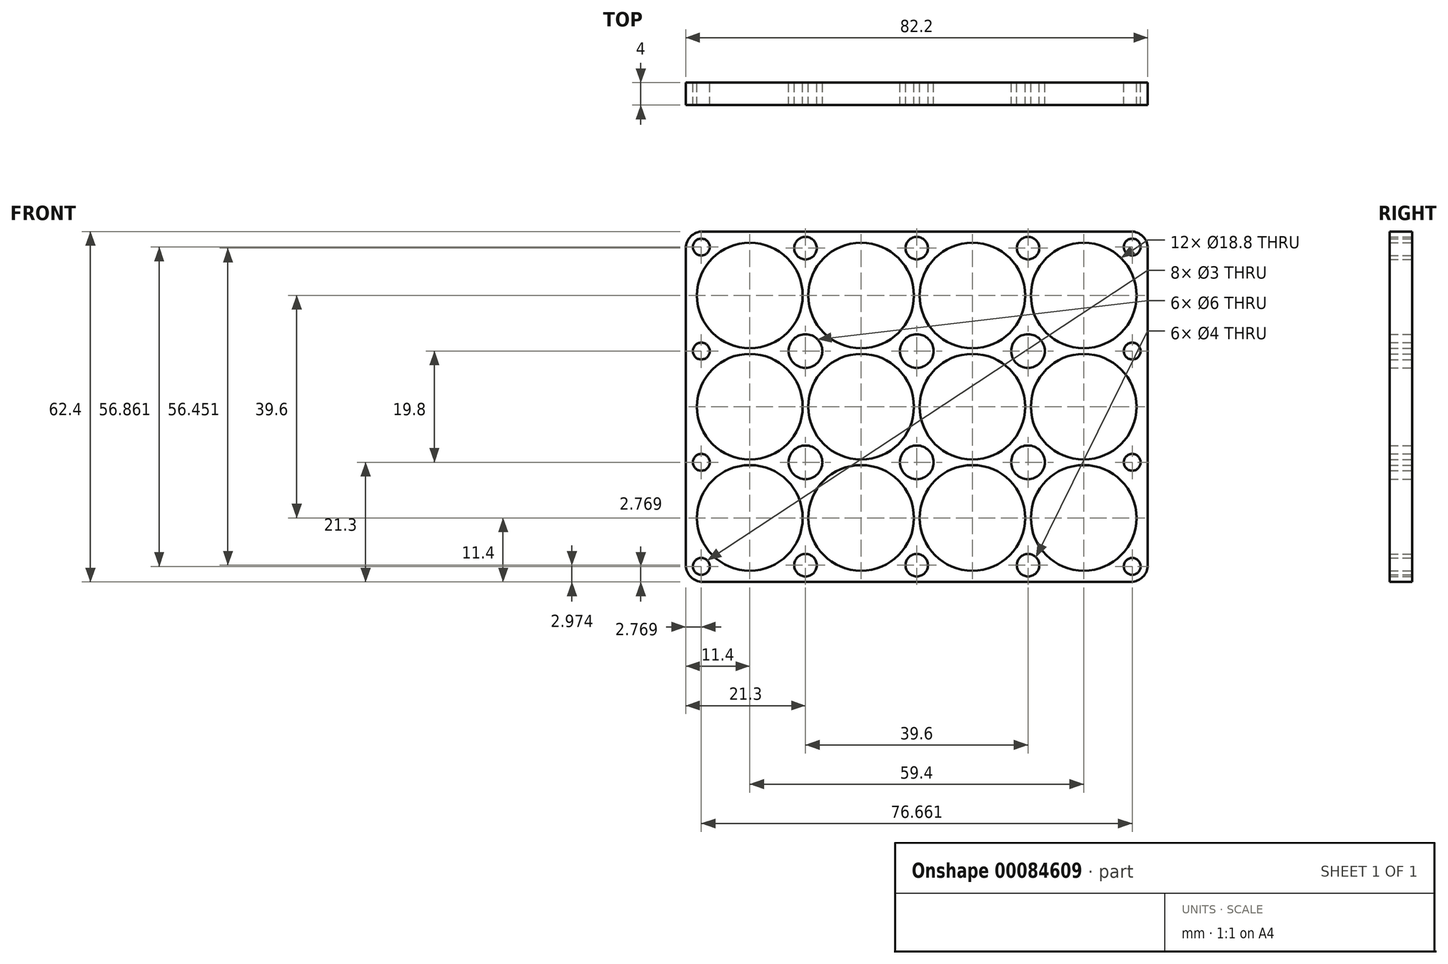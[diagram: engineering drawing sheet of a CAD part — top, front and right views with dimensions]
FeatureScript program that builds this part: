
annotation { "Feature Type Name" : "Feature", "Feature Type Description" : "" }
export const myFeature = defineFeature(function(context is Context, id is Id, definition is map)
    precondition{}
    {
        {
            var Q0;
            Q0=qCreatedBy(makeId("Front.planeOp"),FACE);
            var sketch = newSketch(context, id + "F0", { "sketchPlane" : qUnion([Q0]) });
            skCircle(sketch, "E0", {"center": v(0, 0) * mm, "radius": 9.4 * mm});
            skCircle(sketch, "E1.0.1.0", {"center": v(0, 19.8) * mm, "radius": 9.4 * mm});
            skCircle(sketch, "E1.0.2.0", {"center": v(0, 39.6) * mm, "radius": 9.4 * mm});
            skCircle(sketch, "E1.1.0.0", {"center": v(19.8, 0) * mm, "radius": 9.4 * mm});
            skCircle(sketch, "E1.1.1.0", {"center": v(19.8, 19.8) * mm, "radius": 9.4 * mm});
            skCircle(sketch, "E1.1.2.0", {"center": v(19.8, 39.6) * mm, "radius": 9.4 * mm});
            skCircle(sketch, "E1.2.0.0", {"center": v(39.6, 0) * mm, "radius": 9.4 * mm});
            skCircle(sketch, "E1.2.1.0", {"center": v(39.6, 19.8) * mm, "radius": 9.4 * mm});
            skCircle(sketch, "E1.2.2.0", {"center": v(39.6, 39.6) * mm, "radius": 9.4 * mm});
            skCircle(sketch, "E1.3.0.0", {"center": v(59.4, 0) * mm, "radius": 9.4 * mm});
            skCircle(sketch, "E1.3.1.0", {"center": v(59.4, 19.8) * mm, "radius": 9.4 * mm});
            skCircle(sketch, "E1.3.2.0", {"center": v(59.4, 39.6) * mm, "radius": 9.4 * mm});
            skLineSegment(sketch, "E1.direction1", {"start": v(0, 0) * mm, "end": v(19.8, 0) * mm, "construction": true});
            skLineSegment(sketch, "E1.direction2", {"start": v(0, 0) * mm, "end": v(0, 19.8) * mm, "construction": true});
            skLineSegment(sketch, "E2", {"start": v(-9.4, 19.8) * mm, "end": v(68.8, 19.8) * mm, "construction": true});
            skLineSegment(sketch, "E3", {"start": v(29.7, 19.8) * mm, "end": v(29.7, -16.3) * mm, "construction": true});
            skLineSegment(sketch, "E4.bottom", {"start": v(70.8, -11.4) * mm, "end": v(-11.4, -11.4) * mm});
            skLineSegment(sketch, "E4.top", {"start": v(70.8, 51) * mm, "end": v(-11.4, 51) * mm});
            skLineSegment(sketch, "E4.left", {"start": v(70.8, -11.4) * mm, "end": v(70.8, 51) * mm});
            skLineSegment(sketch, "E4.right", {"start": v(-11.4, -11.4) * mm, "end": v(-11.4, 51) * mm});
            skPoint(sketch, "E4.middle", {"position": v(29.7, 19.8) * mm});
            skLineSegment(sketch, "E5", {"start": v(19.8, 19.8) * mm, "end": v(0, 0) * mm, "construction": true});
            skLineSegment(sketch, "E6", {"start": v(19.8, 0) * mm, "end": v(0, 19.8) * mm, "construction": true});
            skCircle(sketch, "E7", {"center": v(9.9, 9.9) * mm, "radius": 3 * mm});
            skCircle(sketch, "E8.0.1.0", {"center": v(9.9, 29.7) * mm, "radius": 3 * mm});
            skCircle(sketch, "E8.1.0.0", {"center": v(29.7, 9.9) * mm, "radius": 3 * mm});
            skCircle(sketch, "E8.1.1.0", {"center": v(29.7, 29.7) * mm, "radius": 3 * mm});
            skCircle(sketch, "E8.2.0.0", {"center": v(49.5, 9.9) * mm, "radius": 3 * mm});
            skCircle(sketch, "E8.2.1.0", {"center": v(49.5, 29.7) * mm, "radius": 3 * mm});
            skLineSegment(sketch, "E8.direction1", {"start": v(9.9, 9.9) * mm, "end": v(29.7, 9.9) * mm, "construction": true});
            skLineSegment(sketch, "E8.direction2", {"start": v(9.9, 9.9) * mm, "end": v(9.9, 29.7) * mm, "construction": true});
            skLineSegment(sketch, "E9", {"start": v(9.9, 0) * mm, "end": v(9.9, -11.4) * mm, "construction": true});
            skCircle(sketch, "E10", {"center": v(9.9, -8.43) * mm, "radius": 2 * mm});
            skCircle(sketch, "E11.1.0.0", {"center": v(29.7, -8.43) * mm, "radius": 2 * mm});
            skCircle(sketch, "E11.2.0.0", {"center": v(49.5, -8.43) * mm, "radius": 2 * mm});
            skLineSegment(sketch, "E11.direction1", {"start": v(9.9, -8.43) * mm, "end": v(29.7, -8.43) * mm, "construction": true});
            skCircle(sketch, "E12.MirrorC", {"center": v(9.9, 48.03) * mm, "radius": 2 * mm});
            skCircle(sketch, "E13.MirrorC", {"center": v(29.7, 48.03) * mm, "radius": 2 * mm});
            skCircle(sketch, "E14.MirrorC", {"center": v(49.5, 48.03) * mm, "radius": 2 * mm});
            skLineSegment(sketch, "E15", {"start": v(0, 0) * mm, "end": v(-11.4, -11.4) * mm, "construction": true});
            skCircle(sketch, "E16", {"center": v(-8.63, -8.63) * mm, "radius": 1.5 * mm});
            skCircle(sketch, "E17", {"center": v(-8.63, 9.9) * mm, "radius": 1.5 * mm});
            skCircle(sketch, "E18", {"center": v(-8.63, 29.7) * mm, "radius": 1.5 * mm});
            skCircle(sketch, "E19.MirrorC", {"center": v(-8.63, 48.23) * mm, "radius": 1.5 * mm});
            skCircle(sketch, "E20.MirrorC", {"center": v(68.03, -8.63) * mm, "radius": 1.5 * mm});
            skCircle(sketch, "E21.MirrorC", {"center": v(68.03, 9.9) * mm, "radius": 1.5 * mm});
            skCircle(sketch, "E22.MirrorC", {"center": v(68.03, 29.7) * mm, "radius": 1.5 * mm});
            skCircle(sketch, "E23.MirrorC", {"center": v(68.03, 48.23) * mm, "radius": 1.5 * mm});
            skSolve(sketch);
        }
        {
            var Q0;
            Q0 = qSketchRegion(id + "F0", true);
            extrude(context, id + "F1", {"entities" : qUnion([Q0]), "depth" : 4 * mm});
        }
        {
            var Q0;
            Q0=makeQuery(id+"F1.opExtrude","SWEPT_EDGE",EDGE,{"disambiguationData":[OSD([sQuery(id+"F0.wireOp",EDGE,"E4.top"),sQuery(id+"F0.wireOp",EDGE,"E4.left")])]});
            var Q1;
            Q1=makeQuery(id+"F1.opExtrude","SWEPT_EDGE",EDGE,{"disambiguationData":[OSD([sQuery(id+"F0.wireOp",EDGE,"E4.top"),sQuery(id+"F0.wireOp",EDGE,"E4.right")])]});
            var Q2;
            Q2=makeQuery(id+"F1.opExtrude","SWEPT_EDGE",EDGE,{"disambiguationData":[OSD([sQuery(id+"F0.wireOp",EDGE,"E4.bottom"),sQuery(id+"F0.wireOp",EDGE,"E4.right")])]});
            var Q3;
            Q3=makeQuery(id+"F1.opExtrude","SWEPT_EDGE",EDGE,{"disambiguationData":[OSD([sQuery(id+"F0.wireOp",EDGE,"E4.bottom"),sQuery(id+"F0.wireOp",EDGE,"E4.left")])]});
            fillet(context, id + "F2", {"entities" : qUnion([Q0, Q1, Q2, Q3]), "radius" : 3 * mm, "tangentPropagation" : true, "conicFillet" : false});
        }
    });
